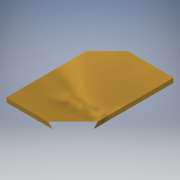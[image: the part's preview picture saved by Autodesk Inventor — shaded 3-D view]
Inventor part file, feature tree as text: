
AUTODESK INVENTOR PART (.ipt)
format: ipt  version: 2016 (Build 200138000, 138)  size: 165,376 bytes
history: native  units: mm
features: other x7, reference x5, sketch x2
ambient origin geometry x8: Origin, YZ Plane, XZ Plane, XY Plane, X Axis, Y Axis, Z Axis, Center Point
bodies: Body1 (feature_tree)
feature tree (14):
  other  "Sólido1"
  other  "Cara1"
  other  "Pestaña1"
  sketch  "Boceto1"  dims[d2=1.0mm]
  reference  "Referencia1"
  reference  "Referencia2"
  other  "Placa1"
  reference  "Referencia3"
  reference  "Referencia4"
  reference  "Referencia5"
  sketch  "Boceto2"  dims[d3=890.475mm d5=890.475mm d6=4.826mm d7=4.826mm d8=4.826mm d9=4.826mm d10=1.0mm d11=0.5mm d12=2.0mm d13=1.0mm d14=38.1mm d15=90.0deg d16=1.0mm d17=4.0mm d18=1.0mm d19=1.0mm]
  other  "Placa2"
  other  "Doblez1"
  other  "Esquina1"
